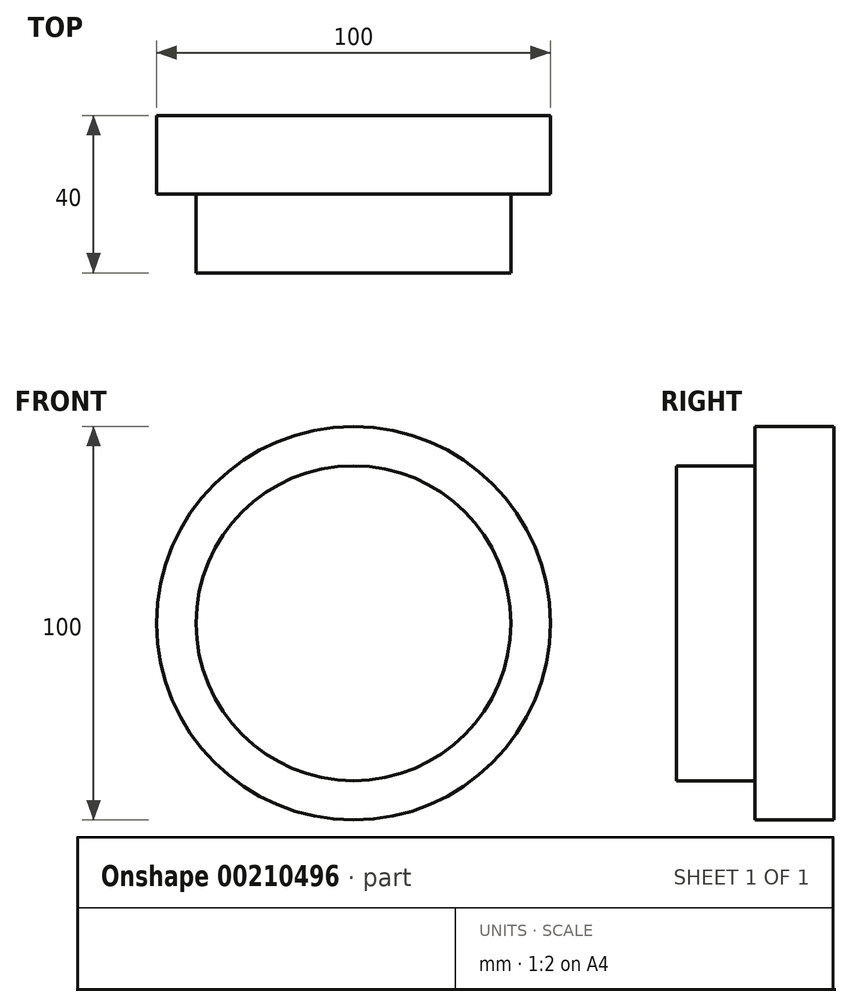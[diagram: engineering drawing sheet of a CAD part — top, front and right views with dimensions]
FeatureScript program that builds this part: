
annotation { "Feature Type Name" : "Feature", "Feature Type Description" : "" }
export const myFeature = defineFeature(function(context is Context, id is Id, definition is map)
    precondition{}
    {
        {
            var Q0;
            Q0=qCreatedBy(makeId("Front.planeOp"),FACE);
            var sketch = newSketch(context, id + "F0", { "sketchPlane" : qUnion([Q0])});
            skCircle(sketch, "E0", {"center": v(0, 0) * mm, "radius": 40 * mm});
            skCircle(sketch, "E1", {"center": v(0, 0) * mm, "radius": 50 * mm});
            skSolve(sketch);
        }
        {
            var Q0;
            Q0=qSketchRegion(id+"F0",true);
            var Q1;
            Q1=makeQuery(id+"F0.imprint","IMPRINT",FACE,{"disambiguationData":[TD([[makeQuery(id+"F0.imprint","IMPRINT",EDGE,{"derivedFrom":sQuery(id+"F0.wireOp",EDGE,"E0")}),-1.0]])]});
            var Q2;
            Q2=makeQuery(id+"F0.imprint","IMPRINT",FACE,{"disambiguationData":[TD([[makeQuery(id+"F0.imprint","IMPRINT",EDGE,{"derivedFrom":sQuery(id+"F0.wireOp",EDGE,"E0")}),1.0]])]});
            extrude(context, id + "F1", {"entities" : qUnion([Q0, Q1, Q2]), "depth" : 20 * mm});
        }
        {
            var Q0;
            Q0=makeQuery(id+"F0.imprint","IMPRINT",FACE,{"disambiguationData":[TD([[makeQuery(id+"F0.imprint","IMPRINT",EDGE,{"derivedFrom":sQuery(id+"F0.wireOp",EDGE,"E0")}),1.0]])]});
            extrude(context, id + "F2", {"entities" : qUnion([Q0]), "operationType" : NewBodyOperationType.ADD, "depth" : 40 * mm});
        }
    });
